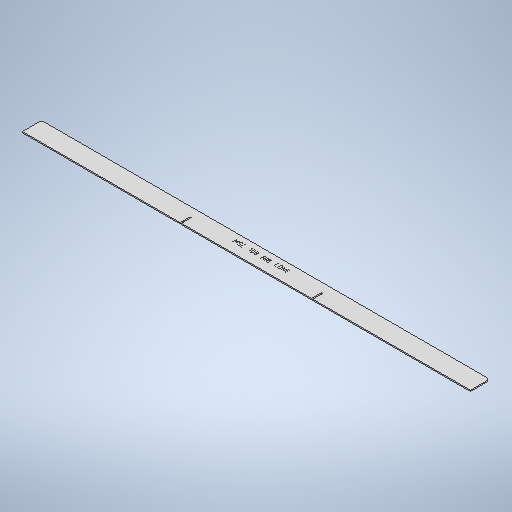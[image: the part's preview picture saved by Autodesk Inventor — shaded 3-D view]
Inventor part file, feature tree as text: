
AUTODESK INVENTOR PART (.ipt)
format: ipt  version: 2025 (Build 290162010, 162A)  size: 383,488 bytes
history: native  units: mm
features: other x5, sketch x3, sheet_metal_op x1, extrude x1
ambient origin geometry x8: Origin, YZ Plane, XZ Plane, XY Plane, X Axis, Y Axis, Z Axis, Center Point
bodies: Body1 (feature_tree)
feature tree (10):
  sheet_metal_op  "Face1"
  extrude  "Extrusion1"  Depth=1170.0mm
  other  "Mark1"
  other  "A-Side Definition"
  other  "Corner Chamfer1"
  sketch  "Sketch1"  dims[d16=50.0mm d17=1170.0mm]
  other  "Plate2"
  sketch  "Sketch2"  dims[d18=50.0mm]
  sketch  "Sketch4"  dims[d19=50.0mm d20=3.0mm d24=0.0mm d25=0.0mm d32=2.0mm d33=8.726646mm d39=26.0mm d41=3.1mm d42=3.0mm d43=340.0mm d45=6.0mm d46=6.0mm d47=45.0deg]
  other  "Definition1"
